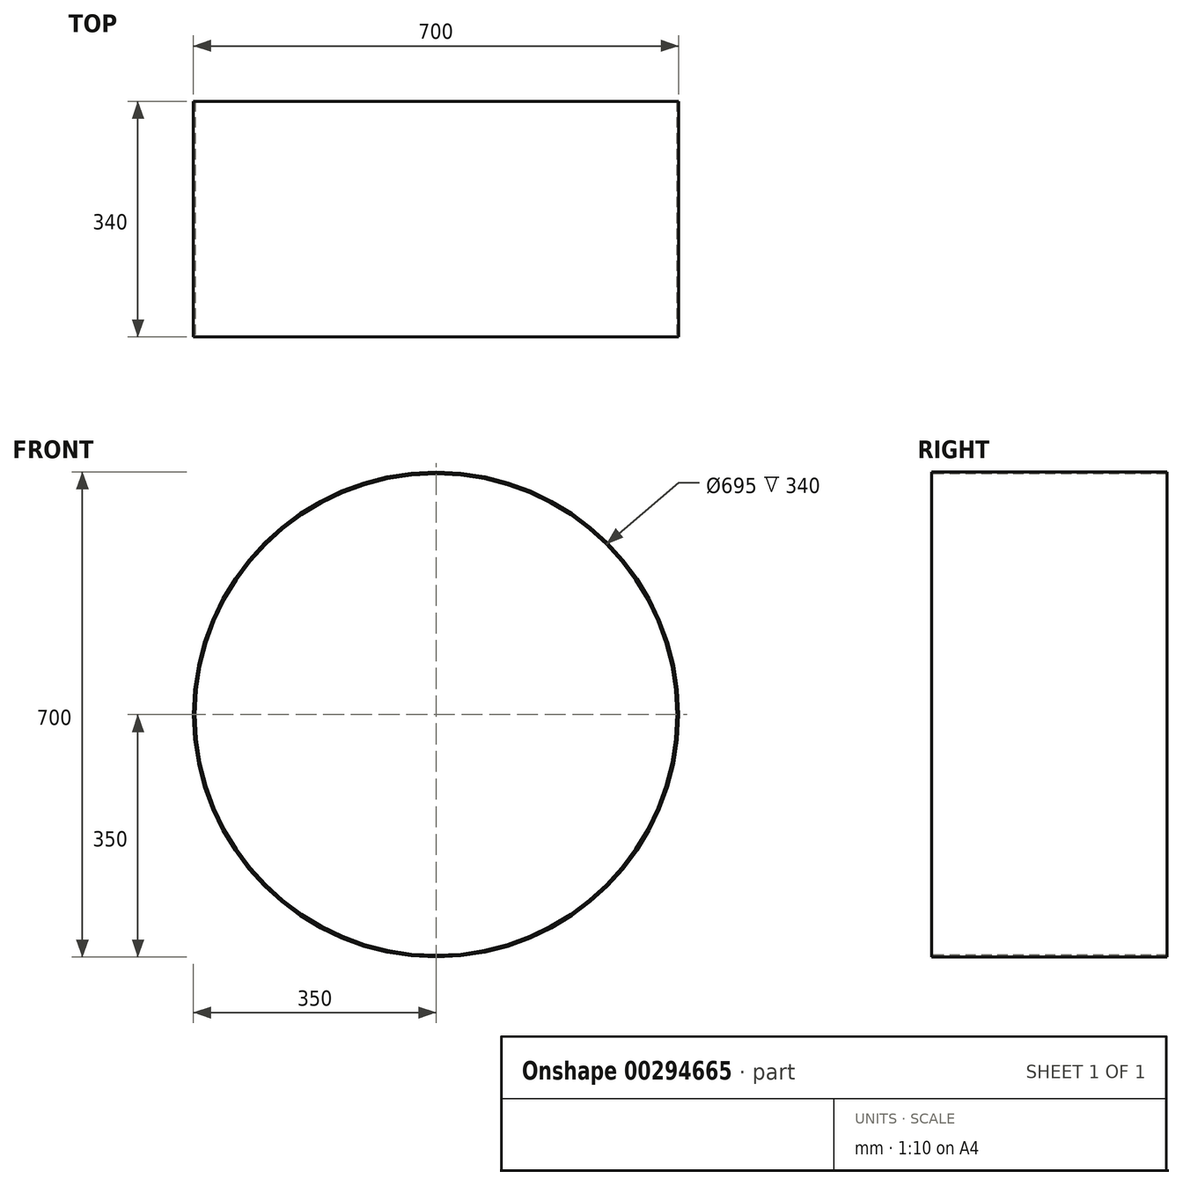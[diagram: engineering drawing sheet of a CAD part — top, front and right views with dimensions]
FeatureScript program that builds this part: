
annotation { "Feature Type Name" : "Feature", "Feature Type Description" : "" }
export const myFeature = defineFeature(function(context is Context, id is Id, definition is map)
    precondition{}
    {
        {
            var Q0;
            Q0=qCreatedBy(makeId("Front.planeOp"),FACE);
            var sketch = newSketch(context, id + "F0", { "sketchPlane" : qUnion([Q0])});
            skCircle(sketch, "E0", {"center": v(0, 0) * mm, "radius": 350 * mm});
            skSolve(sketch);
        }
        {
            var Q0;
            Q0 = qSketchRegion(id + "F0", true);
            extrude(context, id + "F1", {"entities" : qUnion([Q0]), "endBound" : BoundingType.SYMMETRIC, "depth" : 340 * mm});
        }
        {
            var Q0;
            Q0=makeQuery(id+"F1.opExtrude","CAP_FACE",FACE,{"disambiguationData":[OSD([sQuery(id+"F0.wireOp",EDGE,"E0")])],"isStart":false});
            var sketch = newSketch(context, id + "F2", { "sketchPlane" : qUnion([Q0])});
            skCircle(sketch, "E1", {"center": v(0, 0) * mm, "radius": 347.5 * mm});
            skSolve(sketch);
        }
        {
            var Q0;
            Q0 = qSketchRegion(id + "F2", true);
            extrude(context, id + "F3", {"entities" : qUnion([Q0]), "operationType" : NewBodyOperationType.REMOVE, "oppositeDirection" : true, "depth" : 340 * mm});
        }
        {
            var Q0;
            Q0=qCreatedBy(makeId("Front.planeOp"),FACE);
            var sketch = newSketch(context, id + "F4", { "sketchPlane" : qUnion([Q0])});
            skLineSegment(sketch, "E2", {"start": v(0, 0) * mm, "end": v(70.85, 490.89) * mm, "construction": true});
            skLineSegment(sketch, "E3", {"start": v(0, 0) * mm, "end": v(-70.85, 490.89) * mm, "construction": true});
            skCircle(sketch, "E4.0", {"center": v(0, 0) * mm, "radius": 350 * mm, "construction": true});
            skPoint(sketch, "E5", {"position": v(-50, 346.41) * mm});
            skPoint(sketch, "E6", {"position": v(50, 346.41) * mm});
            skSolve(sketch);
        }
        {
            var Q0;
            Q0=qCreatedBy(makeId("Top.planeOp"),FACE);
            var Q1;
            Q1=sQuery(id+"F4.wireOp",VERTEX,"E6");
            cPlane(context, id + "F5", {"entities" : qUnion([Q0, Q1]), "cplaneType" : CPlaneType.PLANE_POINT, "offset" : 25 * mm, "width" : 150 * mm, "height" : 150 * mm});
        }
        {
            var Q0;
            Q0=qCreatedBy(id+"F5.planeOp",FACE);
            var sketch = newSketch(context, id + "F6", { "sketchPlane" : qUnion([Q0])});
            skPoint(sketch, "E7.0", {"position": v(50, 0) * mm});
            skLineSegment(sketch, "E8", {"start": v(50, 0) * mm, "end": v(50, 82.45) * mm, "construction": true});
            skSolve(sketch);
        }
    });
